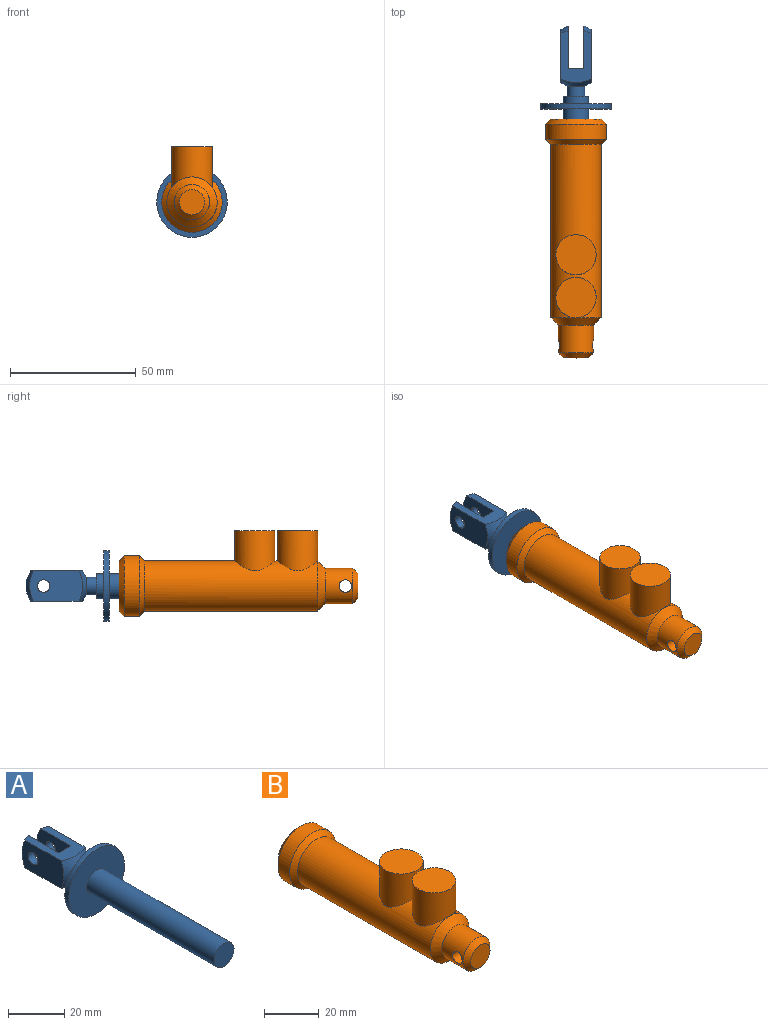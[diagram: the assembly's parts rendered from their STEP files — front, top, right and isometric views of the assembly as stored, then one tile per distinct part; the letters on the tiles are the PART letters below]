
ASSEMBLY  parts=2 mates=1
PART A: 22 faces, bbox 28.4x97.4x28.4 mm
  f0: plane 3.61x0.5mm, normal (0,1,0), area 1.2mm2, adj f1,f20
  f1: cone r=3.5mm half-angle=60deg, axis (0,-1,0), area 40.9mm2, adj f0,f12,f13,f14,f20
  f2: cylinder r=2.5mm len=5mm, axis (1,0,0), area 47.1mm2, adj f14,f20
  f3: plane 10x10mm, normal (0,-1,0), area 78.5mm2, adj f11
  f4: cone r=3.5mm half-angle=60deg, axis (0,1,0), area 121.8mm2, adj f5,f12,f13,f14,f15
  f5: cylinder r=3.5mm len=7mm, axis (0,-1,0), area 88mm2, adj f4,f6
  f6: plane 10x10mm, normal (0,1,0), area 40.1mm2, adj f5,f7
  f7: cylinder r=5mm len=10mm, axis (0,-1,0), area 94.2mm2, adj f6,f8
  f8: plane 28x28mm, normal (0,1,0), area 537.2mm2, adj f7,f9
  f9: cylinder r=14mm len=28mm, axis (0,-1,0), area 175.9mm2, adj f8,f10
  f10: plane 28x28mm, normal (0,-1,0), area 537.2mm2, adj f9,f11
  f11: cylinder r=5mm len=64mm, axis (0,-1,0), area 2010.6mm2, adj f3,f10
  f12: plane 21.08x12.38mm, normal (0,0,1), area 148.6mm2, adj f1,f4,f14,f15,f17,f19,f20,f21
  f13: plane 21.08x12.38mm, normal (0,0,-1), area 148.6mm2, adj f1,f4,f14,f15,f17,f19,f20,f21
  f14: plane 21.11x12.01mm, normal (-1,0,0), area 221.4mm2, adj f1,f2,f4,f12,f13
  f15: plane 21.11x12.01mm, normal (1,0,0), area 221.4mm2, adj f4,f12,f13,f17,f18
  f16: plane 3.61x0.5mm, normal (0,1,0), area 1.2mm2, adj f17,f21
  f17: cone r=3.5mm half-angle=60deg, axis (0,-1,0), area 40.9mm2, adj f12,f13,f15,f16,f21
  f18: cylinder r=2.5mm len=5mm, axis (1,0,0), area 47.1mm2, adj f15,f21
  f19: plane 12x6mm, normal (0,1,0), area 72mm2, adj f12,f13,f20,f21
  f20: plane 17x12mm, normal (1,0,0), area 177.2mm2, adj f0,f1,f2,f12,f13,f19
  f21: plane 17x12mm, normal (-1,0,0), area 177.2mm2, adj f12,f13,f16,f17,f18,f19
PART B: 18 faces, bbox 24x95x34 mm
  f0: cylinder r=10mm len=69mm, axis (0,-1,0), area 3889.2mm2, adj f7,f8,f12,f16
  f1: plane 10x5mm, normal (0,1,0), area 39.3mm2, adj f2,f14
  f2: cylinder r=5mm len=60mm, axis (0,-1,0), area 1678.4mm2, adj f1,f4,f14,f15
  f3: cylinder r=7mm len=14mm, axis (0,-1,0), area 443.8mm2, adj f8,f9,f11
  f4: plane 20x20mm, normal (0,1,0), area 235.6mm2, adj f2,f5
  f5: cone r=12mm half-angle=45deg, axis (0,-1,0), area 195.5mm2, adj f4,f6
  f6: cylinder r=12mm len=24mm, axis (0,-1,0), area 452.4mm2, adj f5,f7
  f7: cone r=10mm half-angle=45deg, axis (0,1,0), area 195.5mm2, adj f0,f6
  f8: cone r=7mm half-angle=45deg, axis (0,1,0), area 226.6mm2, adj f0,f3
  f9: cone r=5mm half-angle=45deg, axis (0,1,0), area 106.6mm2, adj f3,f10
  f10: plane 10x10mm, normal (0,-1,0), area 78.5mm2, adj f9
  f11: cylinder r=2.5mm len=14mm, axis (-1,0,0), area 212.7mm2, adj f3
  f12: cylinder r=8mm len=16mm, axis (0,0,-1), area 697.3mm2, adj f0,f13
  f13: plane 16x16mm, normal (0,0,1), area 201.1mm2, adj f12
  f14: plane 14x10mm, normal (0,0,-1), area 134.4mm2, adj f1,f2,f15
  f15: cylinder r=8mm len=10mm, axis (0,0,-1), area 41.5mm2, adj f2,f14
  f16: cylinder r=8mm len=16mm, axis (0,0,-1), area 697.5mm2, adj f0,f17
  f17: plane 16x16mm, normal (0,0,1), area 201.1mm2, adj f16
PLACE A t=(0,-20,0)mm
PLACE B at identity
MATE slider A.f1 <-> B.f0  axis (0,-1,0) through (0,30,0)mm
